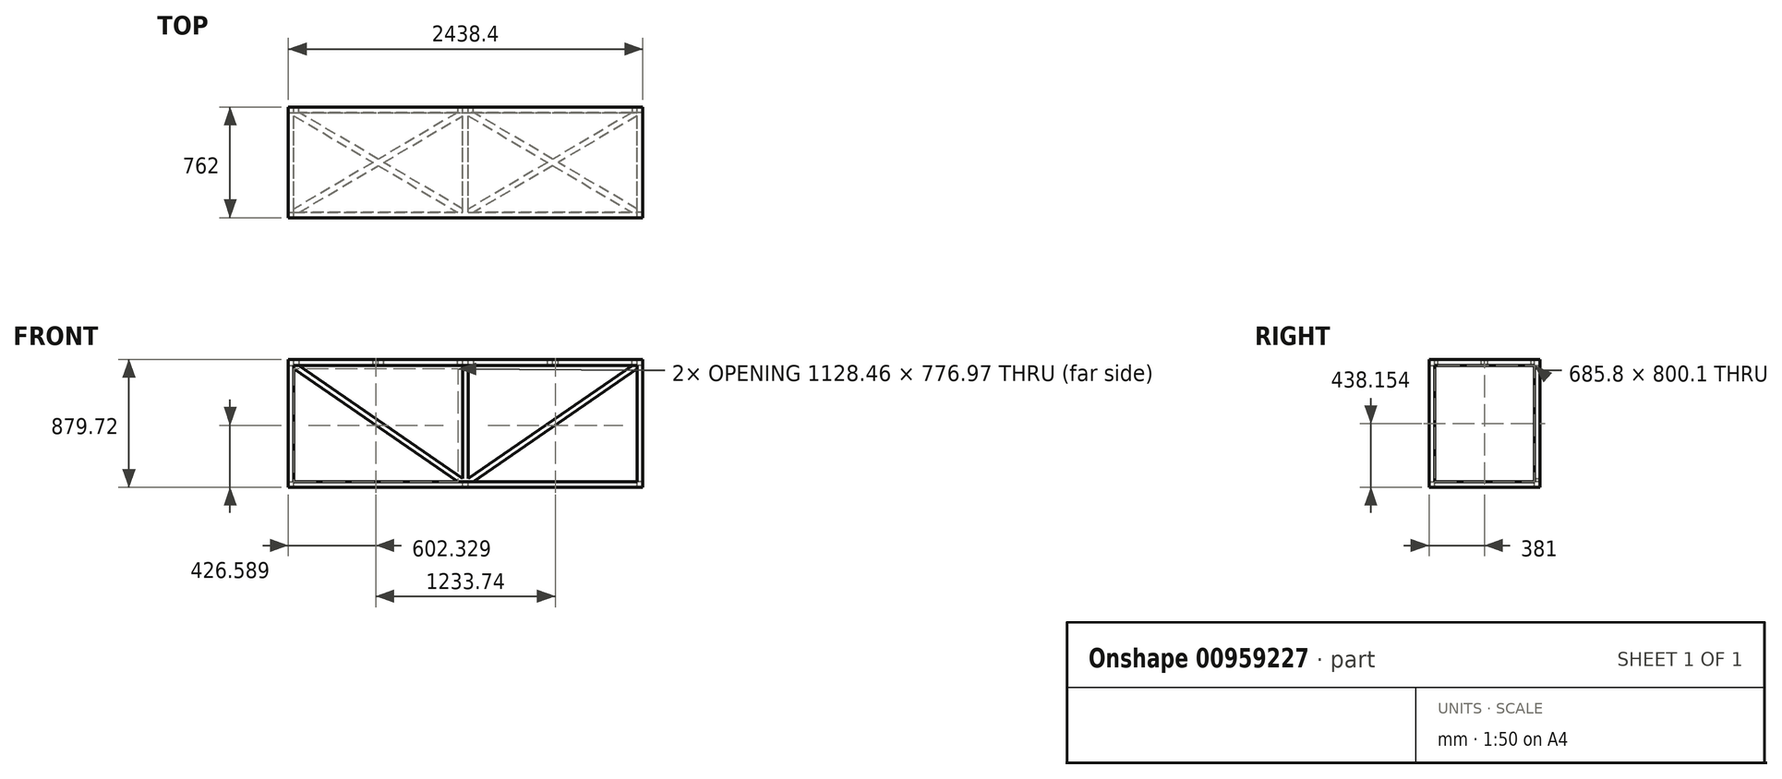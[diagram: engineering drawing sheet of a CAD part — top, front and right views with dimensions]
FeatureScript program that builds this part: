
annotation { "Feature Type Name" : "Feature", "Feature Type Description" : "" }
export const myFeature = defineFeature(function(context is Context, id is Id, definition is map)
    precondition{}
    {
        {
            var Q0;
            Q0=qCreatedBy(makeId("Top.planeOp"),FACE);
            var sketch = newSketch(context, id + "F0", { "sketchPlane" : qUnion([Q0])});
            skLineSegment(sketch, "E0.bottom", {"start": v(1219.2, 381) * mm, "end": v(-1219.2, 381) * mm});
            skLineSegment(sketch, "E0.top", {"start": v(1219.2, -381) * mm, "end": v(-1219.2, -381) * mm});
            skLineSegment(sketch, "E0.left", {"start": v(1219.2, 381) * mm, "end": v(1219.2, -381) * mm});
            skLineSegment(sketch, "E0.right", {"start": v(-1219.2, 381) * mm, "end": v(-1219.2, -381) * mm});
            skPoint(sketch, "E0.middle", {"position": v(0, 0) * mm});
            skSolve(sketch);
        }
        {
            var Q0;
            Q0 = qSketchRegion(id + "F0", true);
            extrude(context, id + "F1", {"entities" : qUnion([Q0]), "oppositeDirection" : true, "depth" : 3.42 * mm, "offsetDistance" : 25.4 * mm});
        }
        {
            var Q0;
            Q0=makeQuery(id+"F1.opExtrude","CAP_FACE",FACE,{"disambiguationData":[OSD([sQuery(id+"F0.wireOp",EDGE,"E0.bottom"),sQuery(id+"F0.wireOp",EDGE,"E0.top"),sQuery(id+"F0.wireOp",EDGE,"E0.left"),sQuery(id+"F0.wireOp",EDGE,"E0.right")])],"isStart":false});
            var sketch = newSketch(context, id + "F2", { "sketchPlane" : qUnion([Q0])});
            skLineSegment(sketch, "E1.bottom", {"start": v(1219.2, 381) * mm, "end": v(-1219.2, 381) * mm});
            skLineSegment(sketch, "E1.top", {"start": v(1219.2, -381) * mm, "end": v(-1219.2, -381) * mm});
            skLineSegment(sketch, "E1.left", {"start": v(1219.2, 381) * mm, "end": v(1219.2, -381) * mm});
            skLineSegment(sketch, "E1.right", {"start": v(-1219.2, 381) * mm, "end": v(-1219.2, -381) * mm});
            skPoint(sketch, "E1.middle", {"position": v(0, 0) * mm});
            skLineSegment(sketch, "E2.bottom", {"start": v(1143.62, 342.9) * mm, "end": v(56.53, 342.9) * mm});
            skLineSegment(sketch, "E2.top", {"start": v(1143.62, -342.9) * mm, "end": v(56.53, -342.9) * mm});
            skLineSegment(sketch, "E2.left", {"start": v(1181.1, 320.78) * mm, "end": v(1181.1, -320.78) * mm});
            skLineSegment(sketch, "E2.right", {"start": v(-1181.1, 320.78) * mm, "end": v(-1181.1, -320.78) * mm});
            skLineSegment(sketch, "E3", {"start": v(-19.05, 320.78) * mm, "end": v(-19.05, -320.78) * mm});
            skLineSegment(sketch, "E4", {"start": v(19.05, 320.78) * mm, "end": v(19.05, -320.78) * mm});
            skLineSegment(sketch, "E5.trimOffspring", {"start": v(-56.53, 342.9) * mm, "end": v(-1143.62, 342.9) * mm});
            skLineSegment(sketch, "E6.trimOffspring", {"start": v(-56.53, -342.9) * mm, "end": v(-1143.62, -342.9) * mm});
            skLineSegment(sketch, "E7", {"start": v(-1181.1, -320.78) * mm, "end": v(-637.56, 0) * mm});
            skLineSegment(sketch, "E8", {"start": v(-19.05, 320.78) * mm, "end": v(-562.6, 0) * mm});
            skPoint(sketch, "E9.orphan", {"position": v(-1181.1, -342.9) * mm});
            skLineSegment(sketch, "E10", {"start": v(-1143.62, 342.9) * mm, "end": v(-600.08, 22.12) * mm});
            skLineSegment(sketch, "E11", {"start": v(-56.53, -342.9) * mm, "end": v(-600.08, -22.12) * mm});
            skPoint(sketch, "E12.orphan", {"position": v(-1181.1, 342.9) * mm});
            skLineSegment(sketch, "E13.trimOffspring", {"start": v(-600.08, -22.12) * mm, "end": v(-1143.62, -342.9) * mm});
            skLineSegment(sketch, "E14.trimOffspring", {"start": v(-637.56, 0) * mm, "end": v(-1181.1, 320.78) * mm});
            skLineSegment(sketch, "E15.trimOffspring", {"start": v(-600.08, 22.12) * mm, "end": v(-56.53, 342.9) * mm});
            skLineSegment(sketch, "E16.trimOffspring", {"start": v(-562.6, 0) * mm, "end": v(-19.05, -320.78) * mm});
            skLineSegment(sketch, "E17", {"start": v(19.05, -320.78) * mm, "end": v(562.6, 0) * mm});
            skLineSegment(sketch, "E18", {"start": v(1181.1, 320.78) * mm, "end": v(637.56, 0) * mm});
            skLineSegment(sketch, "E19", {"start": v(1143.62, -342.9) * mm, "end": v(600.07, -22.12) * mm});
            skLineSegment(sketch, "E20", {"start": v(1181.1, -320.78) * mm, "end": v(637.56, 0) * mm});
            skPoint(sketch, "E21.orphan", {"position": v(1181.1, -342.9) * mm});
            skLineSegment(sketch, "E22.trimOffspring", {"start": v(600.07, -22.12) * mm, "end": v(56.53, -342.9) * mm});
            skLineSegment(sketch, "E23.trimOffspring", {"start": v(600.07, 22.12) * mm, "end": v(1143.62, 342.9) * mm});
            skLineSegment(sketch, "E24.trimOffspring", {"start": v(600.07, 22.12) * mm, "end": v(56.53, 342.9) * mm});
            skLineSegment(sketch, "E25.trimOffspring", {"start": v(562.6, 0) * mm, "end": v(19.05, 320.78) * mm});
            skPoint(sketch, "E26.orphan", {"position": v(1181.1, 342.9) * mm});
            skSolve(sketch);
        }
        {
            var Q0;
            Q0 = qSketchRegion(id + "F2", true);
            extrude(context, id + "F3", {"entities" : qUnion([Q0]), "operationType" : NewBodyOperationType.ADD, "depth" : 38.1 * mm, "offsetDistance" : 25.4 * mm});
        }
        {
            var Q0;
            Q0=makeQuery(id+"F3.opExtrude","CAP_FACE",FACE,{"disambiguationData":[OSD([sQuery(id+"F2.wireOp",EDGE,"E1.bottom"),sQuery(id+"F2.wireOp",EDGE,"E1.top"),sQuery(id+"F2.wireOp",EDGE,"E1.left"),sQuery(id+"F2.wireOp",EDGE,"E1.right"),sQuery(id+"F2.wireOp",EDGE,"E2.bottom"),sQuery(id+"F2.wireOp",EDGE,"E2.top"),sQuery(id+"F2.wireOp",EDGE,"E2.left"),sQuery(id+"F2.wireOp",EDGE,"E2.right"),sQuery(id+"F2.wireOp",EDGE,"E3"),sQuery(id+"F2.wireOp",EDGE,"E4"),sQuery(id+"F2.wireOp",EDGE,"E5.trimOffspring"),sQuery(id+"F2.wireOp",EDGE,"E6.trimOffspring"),sQuery(id+"F2.wireOp",EDGE,"E7"),sQuery(id+"F2.wireOp",EDGE,"E8"),sQuery(id+"F2.wireOp",EDGE,"E10"),sQuery(id+"F2.wireOp",EDGE,"E11"),sQuery(id+"F2.wireOp",EDGE,"E13.trimOffspring"),sQuery(id+"F2.wireOp",EDGE,"E14.trimOffspring"),sQuery(id+"F2.wireOp",EDGE,"E15.trimOffspring"),sQuery(id+"F2.wireOp",EDGE,"E16.trimOffspring"),sQuery(id+"F2.wireOp",EDGE,"E17"),sQuery(id+"F2.wireOp",EDGE,"E18"),sQuery(id+"F2.wireOp",EDGE,"E19"),sQuery(id+"F2.wireOp",EDGE,"E20"),sQuery(id+"F2.wireOp",EDGE,"E22.trimOffspring"),sQuery(id+"F2.wireOp",EDGE,"E23.trimOffspring"),sQuery(id+"F2.wireOp",EDGE,"E24.trimOffspring"),sQuery(id+"F2.wireOp",EDGE,"E25.trimOffspring")])],"isStart":false});
            var sketch = newSketch(context, id + "F4", { "sketchPlane" : qUnion([Q0])});
            skLineSegment(sketch, "E27.bottom", {"start": v(-1219.2, 381) * mm, "end": v(-1181.1, 381) * mm});
            skLineSegment(sketch, "E27.top", {"start": v(-1219.2, 342.9) * mm, "end": v(-1181.1, 342.9) * mm});
            skLineSegment(sketch, "E27.left", {"start": v(-1219.2, 381) * mm, "end": v(-1219.2, 342.9) * mm});
            skLineSegment(sketch, "E27.right", {"start": v(-1181.1, 381) * mm, "end": v(-1181.1, 342.9) * mm});
            skLineSegment(sketch, "E28.bottom", {"start": v(-1219.2, -381) * mm, "end": v(-1181.1, -381) * mm});
            skLineSegment(sketch, "E28.top", {"start": v(-1219.2, -342.9) * mm, "end": v(-1181.1, -342.9) * mm});
            skLineSegment(sketch, "E28.left", {"start": v(-1219.2, -381) * mm, "end": v(-1219.2, -342.9) * mm});
            skLineSegment(sketch, "E28.right", {"start": v(-1181.1, -381) * mm, "end": v(-1181.1, -342.9) * mm});
            skLineSegment(sketch, "E29.bottom", {"start": v(1219.2, -381) * mm, "end": v(1181.1, -381) * mm});
            skLineSegment(sketch, "E29.top", {"start": v(1219.2, -342.9) * mm, "end": v(1181.1, -342.9) * mm});
            skLineSegment(sketch, "E29.left", {"start": v(1219.2, -381) * mm, "end": v(1219.2, -342.9) * mm});
            skLineSegment(sketch, "E29.right", {"start": v(1181.1, -381) * mm, "end": v(1181.1, -342.9) * mm});
            skLineSegment(sketch, "E30.bottom", {"start": v(1219.2, 381) * mm, "end": v(1181.1, 381) * mm});
            skLineSegment(sketch, "E30.top", {"start": v(1219.2, 342.9) * mm, "end": v(1181.1, 342.9) * mm});
            skLineSegment(sketch, "E30.left", {"start": v(1219.2, 381) * mm, "end": v(1219.2, 342.9) * mm});
            skLineSegment(sketch, "E30.right", {"start": v(1181.1, 381) * mm, "end": v(1181.1, 342.9) * mm});
            skSolve(sketch);
        }
        {
            var Q0;
            Q0 = qSketchRegion(id + "F4", true);
            extrude(context, id + "F5", {"entities" : qUnion([Q0]), "operationType" : NewBodyOperationType.ADD, "depth" : 800.1 * mm, "offsetDistance" : 25.4 * mm});
        }
        {
            var Q0;
            Q0=makeQuery(id+"F5.opExtrude","CAP_FACE",FACE,{"disambiguationData":[OSD([sQuery(id+"F4.wireOp",EDGE,"E27.bottom"),sQuery(id+"F4.wireOp",EDGE,"E27.top"),sQuery(id+"F4.wireOp",EDGE,"E27.left"),sQuery(id+"F4.wireOp",EDGE,"E27.right")])],"isStart":false});
            var sketch = newSketch(context, id + "F6", { "sketchPlane" : qUnion([Q0])});
            skLineSegment(sketch, "E31.bottom", {"start": v(-1219.2, 381) * mm, "end": v(1219.2, 381) * mm});
            skLineSegment(sketch, "E31.top", {"start": v(-1219.2, -381) * mm, "end": v(1219.2, -381) * mm});
            skLineSegment(sketch, "E31.left", {"start": v(-1219.2, 381) * mm, "end": v(-1219.2, -381) * mm});
            skLineSegment(sketch, "E31.right", {"start": v(1219.2, 381) * mm, "end": v(1219.2, -381) * mm});
            skLineSegment(sketch, "E32.bottom", {"start": v(-1181.1, 342.9) * mm, "end": v(-19.05, 342.9) * mm});
            skLineSegment(sketch, "E32.top", {"start": v(-1181.1, -342.9) * mm, "end": v(-19.05, -342.9) * mm});
            skLineSegment(sketch, "E32.left", {"start": v(-1181.1, 342.9) * mm, "end": v(-1181.1, -342.9) * mm});
            skLineSegment(sketch, "E32.right", {"start": v(1181.1, 342.9) * mm, "end": v(1181.1, -342.9) * mm});
            skLineSegment(sketch, "E33", {"start": v(-19.05, 342.9) * mm, "end": v(-19.05, -342.9) * mm});
            skLineSegment(sketch, "E34", {"start": v(19.05, 342.9) * mm, "end": v(19.05, -342.9) * mm});
            skLineSegment(sketch, "E35.trimOffspring", {"start": v(19.05, -342.9) * mm, "end": v(1181.1, -342.9) * mm});
            skLineSegment(sketch, "E36.trimOffspring", {"start": v(19.05, 342.9) * mm, "end": v(1181.1, 342.9) * mm});
            skSolve(sketch);
        }
        {
            var Q0;
            Q0 = qSketchRegion(id + "F6", true);
            extrude(context, id + "F7", {"entities" : qUnion([Q0]), "operationType" : NewBodyOperationType.ADD, "depth" : 38.1 * mm, "offsetDistance" : 25.4 * mm});
        }
        {
            var Q0;
            Q0=makeQuery(id+"F1.opExtrude","CAP_VERTEX",VERTEX,{"disambiguationData":[OSD([sQuery(id+"F0.wireOp",EDGE,"E0.bottom"),sQuery(id+"F0.wireOp",EDGE,"E0.right")])],"isStart":true});
            var Q1;
            Q1=makeQuery(id+"F7.opExtrude","CAP_VERTEX",VERTEX,{"disambiguationData":[OSD([sQuery(id+"F6.wireOp",EDGE,"E31.top"),sQuery(id+"F6.wireOp",EDGE,"E31.left")])],"isStart":false});
            var Q2;
            Q2=makeQuery(id+"F7.opExtrude","CAP_VERTEX",VERTEX,{"disambiguationData":[OSD([sQuery(id+"F6.wireOp",EDGE,"E31.top"),sQuery(id+"F6.wireOp",EDGE,"E31.right")])],"isStart":false});
            cPlane(context, id + "F8", {"entities" : qUnion([Q0, Q1, Q2]), "cplaneType" : CPlaneType.THREE_POINT, "offset" : 25.4 * mm, "width" : 152.4 * mm, "height" : 152.4 * mm});
        }
        {
            var Q0;
            Q0=qCreatedBy(id+"F8.planeOp",FACE);
            var sketch = newSketch(context, id + "F9", { "sketchPlane" : qUnion([Q0])});
            skLineSegment(sketch, "E37", {"start": v(19.05, -41.52) * mm, "end": v(19.05, -818.49) * mm});
            skLineSegment(sketch, "E38", {"start": v(-19.05, -41.52) * mm, "end": v(-19.05, -818.49) * mm});
            skLineSegment(sketch, "E39", {"start": v(19.05, -41.52) * mm, "end": v(-19.05, -41.52) * mm});
            skLineSegment(sketch, "E40", {"start": v(19.05, -841.62) * mm, "end": v(-19.05, -841.62) * mm});
            skLineSegment(sketch, "E41", {"start": v(1147.5, -41.52) * mm, "end": v(19.05, -818.49) * mm});
            skLineSegment(sketch, "E42", {"start": v(1181.1, -64.65) * mm, "end": v(52.64, -841.62) * mm});
            skLineSegment(sketch, "E43", {"start": v(1181.1, -64.65) * mm, "end": v(1181.1, -41.52) * mm});
            skLineSegment(sketch, "E44", {"start": v(1181.1, -41.52) * mm, "end": v(1147.5, -41.52) * mm});
            skLineSegment(sketch, "E45", {"start": v(-1147.5, -41.52) * mm, "end": v(-19.05, -818.49) * mm});
            skLineSegment(sketch, "E46", {"start": v(-52.64, -841.62) * mm, "end": v(-1181.1, -64.65) * mm});
            skLineSegment(sketch, "E47", {"start": v(-1147.5, -41.52) * mm, "end": v(-1181.1, -41.52) * mm});
            skLineSegment(sketch, "E48", {"start": v(-1181.1, -41.52) * mm, "end": v(-1181.1, -64.65) * mm});
            skLineSegment(sketch, "E49", {"start": v(52.64, -841.62) * mm, "end": v(19.05, -841.62) * mm});
            skLineSegment(sketch, "E50", {"start": v(-19.05, -841.62) * mm, "end": v(-52.64, -841.62) * mm});
            skSolve(sketch);
        }
        {
            var Q0;
            Q0 = qSketchRegion(id + "F9", true);
            extrude(context, id + "F10", {"entities" : qUnion([Q0]), "operationType" : NewBodyOperationType.ADD, "oppositeDirection" : true, "depth" : 38.1 * mm, "offsetDistance" : 25.4 * mm});
        }
    });
